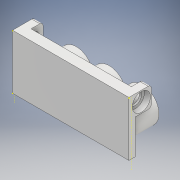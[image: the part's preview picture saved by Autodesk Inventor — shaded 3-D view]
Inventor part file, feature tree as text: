
AUTODESK INVENTOR PART (.ipt)
format: ipt  version: 2018 (Build 220112000, 112)  size: 944,640 bytes
history: native  units: mm
features: sketch x34, extrude x29, fillet x3
ambient origin geometry x8: Origin, YZ Plane, XZ Plane, XY Plane, X Axis, Y Axis, Z Axis, Center Point
bodies: Solid1 (feature_tree)
feature tree (66):
  extrude  "Extrusion1"  Depth=80.0mm
  extrude  "Extrusion2"  Depth=12.0mm
  sketch  "Sketch3"  dims[d5=12.0mm d6=14.5mm]
  extrude  "Extrusion3"  Depth=12.0mm
  extrude  "Extrusion4"  Depth=2.0mm
  extrude  "Extrusion5"  Depth=0.5mm TaperAngle=0.0deg
  sketch  "Sketch7"  dims[d15=10.0mm d16=25.0mm]
  extrude  "Extrusion6"  Depth=25.0mm
  extrude  "Extrusion7"  Depth=25.0mm
  extrude  "Extrusion8"  Depth=10.0mm
  fillet  "Fillet1"  Radius=10.0mm
  fillet  "Fillet2"  Radius=10.0mm
  extrude  "Extrusion9"  Depth=7.5mm TaperAngle=0.0deg
  extrude  "Extrusion10"  Depth=3.0mm
  fillet  "Fillet3"  Radius=3.0mm
  extrude  "Extrusion11"  Depth=21.0mm
  extrude  "Extrusion12"  Depth=41.0mm
  extrude  "Extrusion13"  Depth=42.0mm
  extrude  "Extrusion14"  Depth=38.0mm
  extrude  "Extrusion15"  Depth=45.0mm TaperAngle=0.0deg
  extrude  "Extrusion16"  Depth=3.0mm TaperAngle=0.0deg
  extrude  "Extrusion17"  Depth=3.0mm
  extrude  "Extrusion18"  Depth=39.5mm
  extrude  "Extrusion19"  Depth=45.0mm
  extrude  "Extrusion20"  Depth=125.0mm
  extrude  "Extrusion21"  Depth=1.0mm
  sketch  "Sketch24"  dims[d65=66.0mm d66=3.5mm d67=0.0mm]
  extrude  "Extrusion22"  Depth=10.0mm TaperAngle=0.0deg
  extrude  "Extrusion23"  Depth=12.0mm
  extrude  "Extrusion24"  Depth=3.5mm TaperAngle=0.0deg
  extrude  "Extrusion25"  Depth=2.0mm
  extrude  "Extrusion26"  Depth=2.0mm TaperAngle=0.0deg
  sketch  "Sketch30"  dims[d81=4.0mm]
  extrude  "Extrusion27"  Depth=16.0mm
  extrude  "Extrusion28"  Depth=2.0mm
  extrude  "Extrusion29"  Depth=3.5mm TaperAngle=0.0deg
  sketch  "Sketch34"  dims[d86=15.5mm d87=150.0mm d88=0.0mm d89=12.0mm d90=16.0mm d91=5.0mm d92=16.0mm d93=5.0mm d94=12.0mm d95=3.0mm d96=43.0mm d97=0.0mm d98=43.0mm d99=0.0mm d100=38.75mm d101=38.75mm d102=5.0mm d103=0.0mm d104=500.0mm d105=0.0mm d106=45.0mm d107=0.0mm d108=45.0mm d109=0.0mm d110=38.75mm d111=38.75mm d112=45.0mm d113=0.0mm d114=3.5mm d115=0.0mm d116=43.0mm d117=0.0mm]
  sketch  "Sketch1"  dims[d0=145.0mm d1=80.0mm]
  sketch  "Sketch2"  dims[d2=3.0mm d3=0.0mm d4=12.0mm]
  sketch  "Sketch4"  dims[d7=2.0mm d8=2.0mm]
  sketch  "Sketch5"  dims[d9=6.0mm d10=0.0mm d11=0.5mm d12=0.0mm]
  sketch  "Sketch6"  dims[d13=10.0mm d14=25.0mm]
  sketch  "Sketch8"  dims[d17=25.0mm d18=0.0mm d19=22.5mm d20=10.0mm d21=0.0mm d22=10.0mm]
  sketch  "Sketch9"  dims[d23=2.5mm d24=0.0mm d25=7.5mm d26=0.0mm]
  sketch  "Sketch10"  dims[d27=10.0mm d28=0.0mm d29=4.0mm d30=3.0mm]
  sketch  "Sketch11"  dims[d31=1.0mm d32=21.0mm]
  sketch  "Sketch12"  dims[d33=38.0mm d34=41.0mm]
  sketch  "Sketch13"  dims[d35=38.0mm d36=42.0mm]
  sketch  "Sketch14"  dims[d37=41.0mm d38=38.0mm]
  sketch  "Sketch15"  dims[d39=42.0mm d40=45.0mm d41=0.0mm]
  sketch  "Sketch16"  dims[d42=12.5mm d43=3.0mm d44=0.0mm]
  sketch  "Sketch17"  dims[d45=3.0mm d46=39.5mm]
  sketch  "Sketch18"  dims[d47=39.5mm d48=39.5mm]
  sketch  "Sketch19"  dims[d49=45.0mm d50=0.0mm d51=7.25mm]
  sketch  "Sketch20"  dims[d52=4.0mm d53=7.75mm d54=0.0mm d55=0.0mm d56=125.0mm]
  sketch  "Sketch21"  dims[d57=10.0mm d58=0.0mm d59=1.0mm]
  sketch  "Sketch22"  dims[d60=14.5mm d61=10.0mm d62=0.0mm]
  sketch  "Sketch23"  dims[d63=16.0mm d64=12.0mm]
  sketch  "Sketch25"  dims[d68=4.0mm d69=2.0mm]
  sketch  "Sketch26"  dims[d70=4.0mm d71=2.0mm d72=0.0mm]
  sketch  "Sketch27"  dims[d73=2.0mm d74=0.0mm d75=16.0mm]
  sketch  "Sketch28"  dims[d76=2.0mm d77=2.0mm]
  sketch  "Sketch29"  dims[d78=2.0mm d79=3.5mm d80=0.0mm]
  sketch  "Sketch31"  dims[d82=4.0mm]
  sketch  "Sketch32"  dims[d83=4.0mm]
  sketch  "Sketch33"  dims[d84=2.0mm d85=0.0mm]
